# Revit family: 2060565 Sylvania Lighting Fixture ASCENT 100 II ARCH 2700 4K STD 160
name_source: partatom
category: Lighting Fixtures
revit_build: Autodesk Revit 2016 (Build: 20150220_1215(x64)
units: mm (PartAtom-declared; Revit-internal decimal feet)

## family parameters
Cut with Voids When Loaded = No
Host = Face
Light Source = Yes
OmniClass Number = 23.80.70.11.17
OmniClass Title = Specialized Lighting by Location or Use
Part Type = Normal
Room Calculation Point = No
Round Connector Dimension = Use Diameter
Shared = No

## types (1)
- 2060565 ASCT100 II ARCH 2700 4K STD 160
    Aperture_SYL = 160 mm  [stored 0.524934 ft]
    Apparent Load = 21 VA
    Assembly Code = D5020200
    AssetType = Fixed
    Color Filter = 16777215
    CutoutDiameter_SYL = 176 mm
    Default Elevation = 0 mm  [stored 0 ft]
    Description = Direct LED retro fit for original LED 100 Arch (160) single CFL lamp offering Matching lumen levels and improved light distribution of original LED 100 CFL lamp equivalents Typically half the power consumption compared to CFL Up to 112lm/W 160mm aperture Architectural reflector accepts range of glass accessories from existing LED 100 Arch 160 offering HE, HO and VHO versions equivalent of single 1 x 18W, 1 x 32W, 1 x 42W
 Additional VVHO versions which offer the performance circa 2 x 32W equivalent
    Diameter_SYL = 189 mm  [stored 0.620079 ft]
    DiffuserRadius_SYL = 73 mm  [stored 0.239501 ft]
    Dimming Lamp Color Temperature Shift = <None>
    DocumentationLiterature = http://www.sylvania-lighting.com
    DurationUnit = hours
    ElectricShockClassification = Class II
    Emit Shape Visible in Rendering = No
    Emit from Circle Diameter = 146 mm  [stored 0.479003 ft]
    EmittionSurface_SYL = 3 mm  [stored 0.00984252 ft]
    ExpectedLife = 50000
    HeightAcc_SYL = 7 mm  [stored 0.0229659 ft]
    Height_SYL = 94 mm  [stored 0.308399 ft]
    IfcExportAs = IfcLightFixtureType
    IfcExportType = IfcLightFixtureType
    ImpactProtectionIndex = IK02
    IngressProtection = IP40
    Keynote = 16500
    Lamp = LED
    LampColourRenderingIndex = 80
    LampColourTemperature = 4000 K
    LampMacAdamStep = 3
    LampNominalLuminous = 2767 lm
    LampsType = LED
    LightOutputRatio = 100
    LuminousEfficacy = 132 lm/W
    Manufacturer = Feilo Sylvania
    ManufacturerName = Feilo Sylvania
    Material = aluminium housing, arcylic diffuser
    Material_1_SYL = Aluminum_Sylvania_Ascent_White
    Material_2_SYL = Aluminium_Sylvania_Ascent_Silver
    Material_3_SYL = Polycarbonate_Sylvania_Ascent_Opal
    Material_4_SYL = <By Category>
    Model = ASCENT 100 II ARCH 2700 4K STD 160
    ModelNumber = 2060565
    ModelReference = ASCENT 100 II ARCH 2700 4K STD 160
    Name = ASCENT 100 II ARCH 2700 4K STD 160
    NominalHeight = 94 mm  [stored 0.308399 ft]
    NominalLength = 0 mm  [stored 0 ft]
    NominalWidth = 0 mm  [stored 0 ft]
    Photometric Web File = 2060565.ies
    PowerConsumption = 21 W
    PowerFactor = 0
    RadiusAcc_SYL = 105 mm  [stored 0.344488 ft]
    Radius_SYL = 94.5 mm  [stored 0.310039 ft]
    ReflectorRadius_SYL = 80 mm  [stored 0.262467 ft]
    Tilt Angle = -90°
    TypeName = ASCENT 100 II ARCH 2700 4K STD 160
    URL = http://www.sylvania-lighting.com
    VisibilityAccessory_SYL = No
    Voltage = 0 V
    Weight = 1.2 kg
    WidthBezelAcc_SYL = 25 mm  [stored 0.082021 ft]

note: [stored X ft] marks values corroborated as IEEE doubles in the binary element streams (Revit-internal decimal feet)

## geometry (parser evidence)
native form markers: Sweep x3
no freeform markers — native parametric forms only
